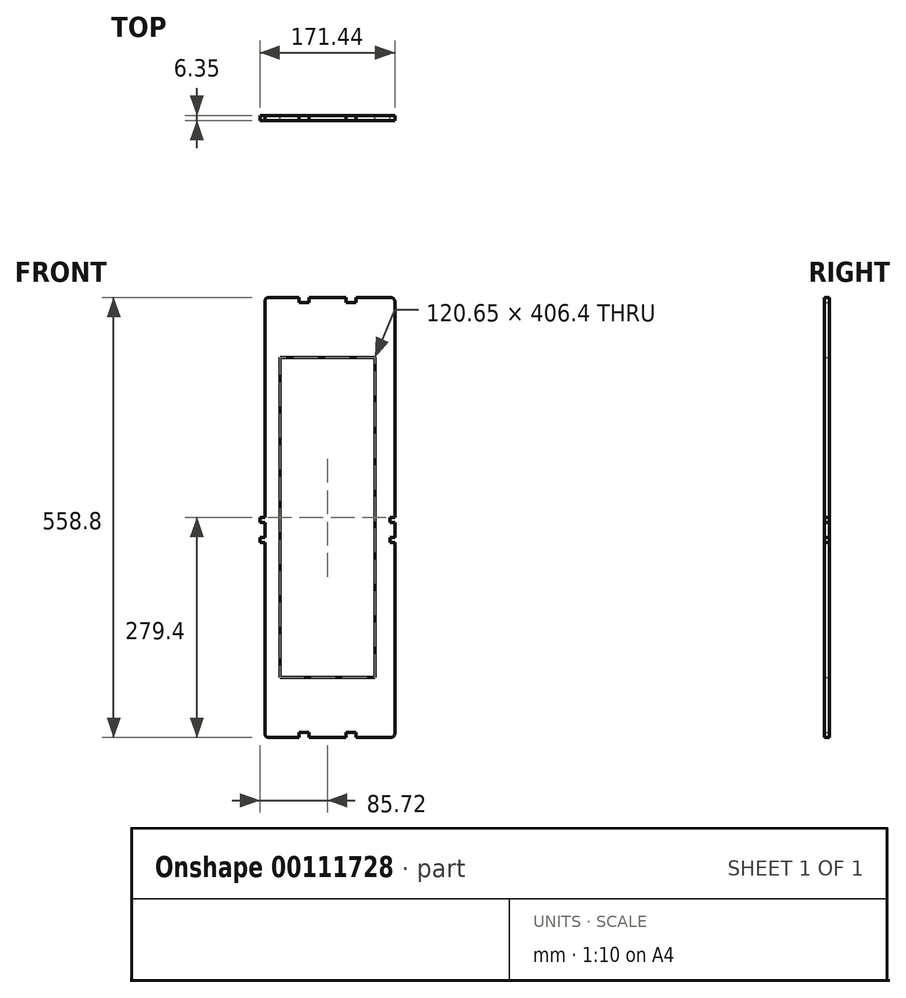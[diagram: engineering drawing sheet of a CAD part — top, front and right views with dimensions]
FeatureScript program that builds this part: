
annotation { "Feature Type Name" : "Feature", "Feature Type Description" : "" }
export const myFeature = defineFeature(function(context is Context, id is Id, definition is map)
    precondition{}
    {
        {
            var Q0;
            Q0=qCreatedBy(makeId("Front.planeOp"),FACE);
            var sketch = newSketch(context, id + "F0", { "sketchPlane" : qUnion([Q0])});
            skLineSegment(sketch, "E0.bottom", {"start": v(85.73, 279.4) * mm, "end": v(36.16, 279.4) * mm});
            skLineSegment(sketch, "E0.top", {"start": v(85.72, -279.4) * mm, "end": v(36.16, -279.4) * mm});
            skLineSegment(sketch, "E0.left", {"start": v(85.73, 279.4) * mm, "end": v(85.73, 0) * mm});
            skLineSegment(sketch, "E0.right", {"start": v(-85.73, 279.4) * mm, "end": v(-85.73, -279.4) * mm, "construction": true});
            skPoint(sketch, "E0.middle", {"position": v(0, 0) * mm});
            skLineSegment(sketch, "E1.bottom", {"start": v(60.33, 203.2) * mm, "end": v(-60.33, 203.2) * mm});
            skLineSegment(sketch, "E1.top", {"start": v(60.33, -203.2) * mm, "end": v(-60.33, -203.2) * mm});
            skLineSegment(sketch, "E1.left", {"start": v(60.33, 203.2) * mm, "end": v(60.33, -203.2) * mm});
            skLineSegment(sketch, "E1.right", {"start": v(-60.33, 203.2) * mm, "end": v(-60.33, -203.2) * mm});
            skLineSegment(sketch, "E2", {"start": v(0, 203.2) * mm, "end": v(0, 279.4) * mm, "construction": true});
            skLineSegment(sketch, "E3", {"start": v(60.33, 0) * mm, "end": v(85.73, 0) * mm, "construction": true});
            skLineSegment(sketch, "E4", {"start": v(0, 0) * mm, "end": v(-85.73, 0) * mm, "construction": true});
            skLineSegment(sketch, "E5", {"start": v(-85.73, 0) * mm, "end": v(-85.73, -6.35) * mm});
            skLineSegment(sketch, "E6", {"start": v(-85.72, -6.35) * mm, "end": v(-79.38, -6.35) * mm});
            skLineSegment(sketch, "E7", {"start": v(-79.38, -6.35) * mm, "end": v(-79.38, -25.4) * mm});
            skLineSegment(sketch, "E8", {"start": v(-79.38, -25.4) * mm, "end": v(-85.73, -25.4) * mm});
            skLineSegment(sketch, "E9", {"start": v(-85.73, -25.4) * mm, "end": v(-85.73, -31.75) * mm});
            skLineSegment(sketch, "E10", {"start": v(-85.73, -31.75) * mm, "end": v(-79.38, -31.75) * mm});
            skLineSegment(sketch, "E11", {"start": v(-79.38, -31.75) * mm, "end": v(-79.38, -279.4) * mm});
            skLineSegment(sketch, "E12", {"start": v(-85.73, 0) * mm, "end": v(-79.38, 0) * mm});
            skLineSegment(sketch, "E13", {"start": v(-79.38, 0) * mm, "end": v(-79.38, 279.4) * mm});
            skLineSegment(sketch, "E14", {"start": v(0, 0) * mm, "end": v(0, 203.2) * mm, "construction": true});
            skLineSegment(sketch, "E15.MirrorCS", {"start": v(85.73, 0) * mm, "end": v(79.38, 0) * mm});
            skLineSegment(sketch, "E16.MirrorCS", {"start": v(85.72, -6.35) * mm, "end": v(79.38, -6.35) * mm});
            skLineSegment(sketch, "E17.MirrorCS", {"start": v(85.73, -31.75) * mm, "end": v(79.38, -31.75) * mm});
            skLineSegment(sketch, "E18.MirrorCS", {"start": v(79.38, -25.4) * mm, "end": v(85.73, -25.4) * mm});
            skLineSegment(sketch, "E19", {"start": v(79.38, 0) * mm, "end": v(79.38, -6.35) * mm});
            skLineSegment(sketch, "E20", {"start": v(79.38, -25.4) * mm, "end": v(79.38, -31.75) * mm});
            skLineSegment(sketch, "E21.trimOffspring", {"start": v(85.73, -6.35) * mm, "end": v(85.73, -25.4) * mm});
            skLineSegment(sketch, "E22.trimOffspring", {"start": v(85.73, -31.75) * mm, "end": v(85.73, -279.4) * mm});
            skLineSegment(sketch, "E23", {"start": v(-29.8, 273.05) * mm, "end": v(29.8, 273.05) * mm, "construction": true});
            skLineSegment(sketch, "E24", {"start": v(-36.16, 279.4) * mm, "end": v(-36.16, 273.05) * mm});
            skLineSegment(sketch, "E25", {"start": v(-36.16, 273.05) * mm, "end": v(-23.46, 273.05) * mm});
            skLineSegment(sketch, "E26", {"start": v(-23.46, 273.05) * mm, "end": v(-23.46, 279.4) * mm});
            skLineSegment(sketch, "E27.MirrorCS", {"start": v(23.46, 273.05) * mm, "end": v(23.46, 279.4) * mm});
            skLineSegment(sketch, "E28.MirrorCS", {"start": v(36.16, 273.05) * mm, "end": v(23.46, 273.05) * mm});
            skLineSegment(sketch, "E29.MirrorCS", {"start": v(36.16, 279.4) * mm, "end": v(36.16, 273.05) * mm});
            skLineSegment(sketch, "E30.trimOffspring", {"start": v(-36.16, 279.4) * mm, "end": v(-85.73, 279.4) * mm});
            skLineSegment(sketch, "E31.trimOffspring", {"start": v(23.46, 279.4) * mm, "end": v(-23.46, 279.4) * mm});
            skLineSegment(sketch, "E32.MirrorCS", {"start": v(36.16, -279.4) * mm, "end": v(36.16, -273.05) * mm});
            skLineSegment(sketch, "E33.MirrorCS", {"start": v(23.46, -273.05) * mm, "end": v(23.46, -279.4) * mm});
            skLineSegment(sketch, "E34.MirrorCS", {"start": v(36.16, -273.05) * mm, "end": v(23.46, -273.05) * mm});
            skLineSegment(sketch, "E35.MirrorCS", {"start": v(-23.46, -273.05) * mm, "end": v(-23.46, -279.4) * mm});
            skLineSegment(sketch, "E36.MirrorCS", {"start": v(-36.16, -273.05) * mm, "end": v(-23.46, -273.05) * mm});
            skLineSegment(sketch, "E37.MirrorCS", {"start": v(-36.16, -279.4) * mm, "end": v(-36.16, -273.05) * mm});
            skLineSegment(sketch, "E38.trimOffspring", {"start": v(-36.16, -279.4) * mm, "end": v(-85.72, -279.4) * mm});
            skLineSegment(sketch, "E39.trimOffspring", {"start": v(23.46, -279.4) * mm, "end": v(-23.46, -279.4) * mm});
            skSolve(sketch);
        }
        {
            var Q0;
            Q0 = qSketchRegion(id + "F0", true);
            extrude(context, id + "F1", {"entities" : qUnion([Q0]), "depth" : 6.35 * mm});
        }
        {
            var Q0;
            Q0=makeQuery(id+"F1.opExtrude","SWEPT_EDGE",EDGE,{"disambiguationData":[OSD([sQuery(id+"F0.wireOp",EDGE,"E0.bottom"),sQuery(id+"F0.wireOp",EDGE,"E0.left")])]});
            var Q1;
            Q1=makeQuery(id+"F1.opExtrude","SWEPT_EDGE",EDGE,{"disambiguationData":[OSD([sQuery(id+"F0.wireOp",EDGE,"E13"),sQuery(id+"F0.wireOp",EDGE,"E30.trimOffspring")])]});
            var Q2;
            Q2=makeQuery(id+"F1.opExtrude","SWEPT_EDGE",EDGE,{"disambiguationData":[OSD([sQuery(id+"F0.wireOp",EDGE,"E0.bottom"),sQuery(id+"F0.wireOp",EDGE,"E0.left")])]});
            var Q3;
            Q3=makeQuery(id+"F1.opExtrude","SWEPT_EDGE",EDGE,{"disambiguationData":[OSD([sQuery(id+"F0.wireOp",EDGE,"E0.top"),sQuery(id+"F0.wireOp",EDGE,"E22.trimOffspring")])]});
            var Q4;
            Q4=makeQuery(id+"F1.opExtrude","SWEPT_EDGE",EDGE,{"disambiguationData":[OSD([sQuery(id+"F0.wireOp",EDGE,"E0.top"),sQuery(id+"F0.wireOp",EDGE,"E22.trimOffspring")])]});
            var Q5;
            Q5=makeQuery(id+"F1.opExtrude","SWEPT_EDGE",EDGE,{"disambiguationData":[OSD([sQuery(id+"F0.wireOp",EDGE,"E11"),sQuery(id+"F0.wireOp",EDGE,"E38.trimOffspring")])]});
            fillet(context, id + "F2", {"entities" : qUnion([Q0, Q1, Q2, Q3, Q4, Q5]), "radius" : 5.08 * mm, "tangentPropagation" : true, "allowEdgeOverflow" : false});
        }
    });
